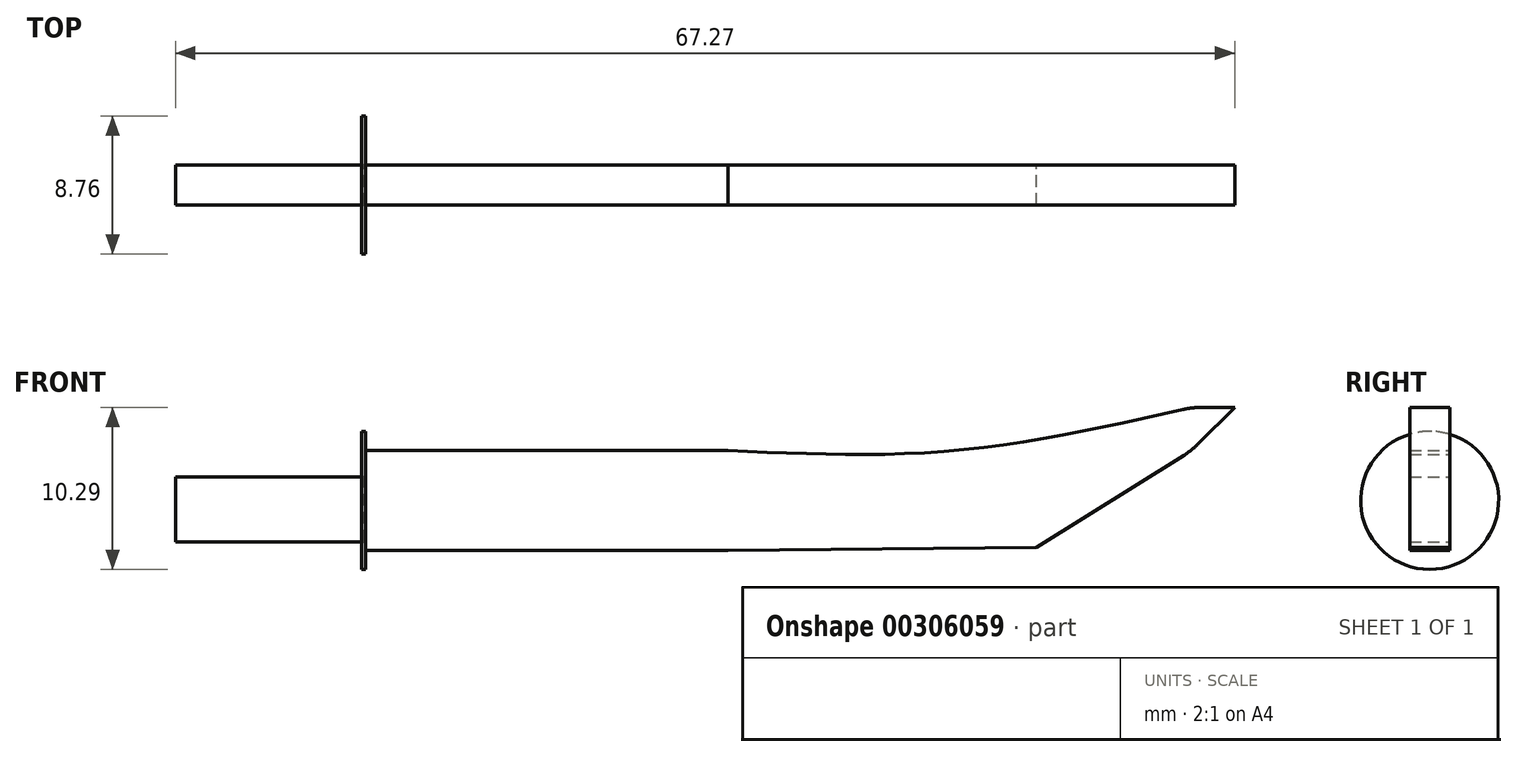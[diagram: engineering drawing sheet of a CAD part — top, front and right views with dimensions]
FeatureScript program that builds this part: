
annotation { "Feature Type Name" : "Feature", "Feature Type Description" : "" }
export const myFeature = defineFeature(function(context is Context, id is Id, definition is map)
    precondition{}
    {
        {
            var Q0;
            Q0=qCreatedBy(makeId("Front.planeOp"),FACE);
            var sketch = newSketch(context, id + "F0", { "sketchPlane" : qUnion([Q0])});
            skLineSegment(sketch, "E0", {"start": v(-62.45, 44.03) * mm, "end": v(-62.45, 37.7) * mm});
            skLineSegment(sketch, "E1", {"start": v(-62.45, 37.7) * mm, "end": v(-39.43, 37.7) * mm});
            skLineSegment(sketch, "E2", {"start": v(-39.43, 37.7) * mm, "end": v(-39.43, 44.03) * mm});
            skLineSegment(sketch, "E3", {"start": v(-62.45, 44.03) * mm, "end": v(-39.43, 44.03) * mm});
            skLineSegment(sketch, "E4", {"start": v(-39.43, 37.7) * mm, "end": v(-19.84, 37.88) * mm});
            skLineSegment(sketch, "E5", {"start": v(-9.98, 44.03) * mm, "end": v(-19.84, 37.88) * mm});
            skFitSpline(sketch, "E6", {"points": [v(-39.43, 44.03) * mm, v(-25, 44.03) * mm, v(-9.98, 46.77) * mm], "startDerivative": vector(29.18, -1.33) * mm, "endDerivative": vector(29.71, 6.76) * mm});
            skLineSegment(sketch, "E7", {"start": v(-9.98, 44.03) * mm, "end": v(-7.24, 46.77) * mm});
            skLineSegment(sketch, "E8", {"start": v(-7.24, 46.77) * mm, "end": v(-9.98, 46.77) * mm});
            skSolve(sketch);
        }
        {
            var Q0;
            Q0 = qSketchRegion(id + "F0", true);
            extrude(context, id + "F1", {"entities" : qUnion([Q0]), "depth" : 2.54 * mm});
        }
        {
            var Q0;
            Q0=makeQuery(id+"F1.opExtrude","SWEPT_FACE",FACE,{"disambiguationData":[OSD([sQuery(id+"F0.wireOp",EDGE,"E0")])]});
            var sketch = newSketch(context, id + "F2", { "sketchPlane" : qUnion([Q0])});
            skCircle(sketch, "E9", {"center": v(1.27, 40.87) * mm, "radius": 4.38 * mm});
            skPoint(sketch, "E9.centerSnap0", {"position": v(0, 40.87) * mm});
            skPoint(sketch, "E9.centerSnap1", {"position": v(1.27, 37.7) * mm});
            skSolve(sketch);
        }
        {
            var Q0;
            Q0 = qSketchRegion(id + "F2", true);
            extrude(context, id + "F3", {"entities" : qUnion([Q0]), "operationType" : NewBodyOperationType.ADD, "depth" : 0.25 * mm});
        }
        {
            var Q0;
            Q0=qCreatedBy(makeId("Front.planeOp"),FACE);
            var sketch = newSketch(context, id + "F4", { "sketchPlane" : qUnion([Q0])});
            skLineSegment(sketch, "E10", {"start": v(-74.5, 38.24) * mm, "end": v(-62.52, 38.24) * mm});
            skLineSegment(sketch, "E11", {"start": v(-62.52, 38.24) * mm, "end": v(-62.52, 42.34) * mm});
            skLineSegment(sketch, "E12", {"start": v(-62.52, 42.34) * mm, "end": v(-74.5, 42.34) * mm});
            skLineSegment(sketch, "E13", {"start": v(-74.5, 38.24) * mm, "end": v(-74.5, 42.34) * mm});
            skSolve(sketch);
        }
        {
            var Q0;
            Q0 = qSketchRegion(id + "F4", true);
            extrude(context, id + "F5", {"entities" : qUnion([Q0]), "depth" : 2.54 * mm});
        }
        {
            var Q0;
            Q0=makeQuery(id+"F1.opExtrude","SWEPT_EDGE",EDGE,{"disambiguationData":[OSD([sQuery(id+"F0.wireOp",EDGE,"E5"),sQuery(id+"F0.wireOp",EDGE,"E7")])]});
            fillet(context, id + "F6", {"entities" : qUnion([Q0]), "radius" : 5.08 * mm, "tangentPropagation" : true, "allowEdgeOverflow" : false});
        }
        {
            var Q0;
            Q0=makeQuery(id+"F1.opExtrude","SWEPT_EDGE",EDGE,{"disambiguationData":[OSD([sQuery(id+"F0.wireOp",EDGE,"E6"),sQuery(id+"F0.wireOp",EDGE,"E8")])]});
            fillet(context, id + "F7", {"entities" : qUnion([Q0]), "radius" : 5.08 * mm, "tangentPropagation" : true, "allowEdgeOverflow" : false});
        }
    });
